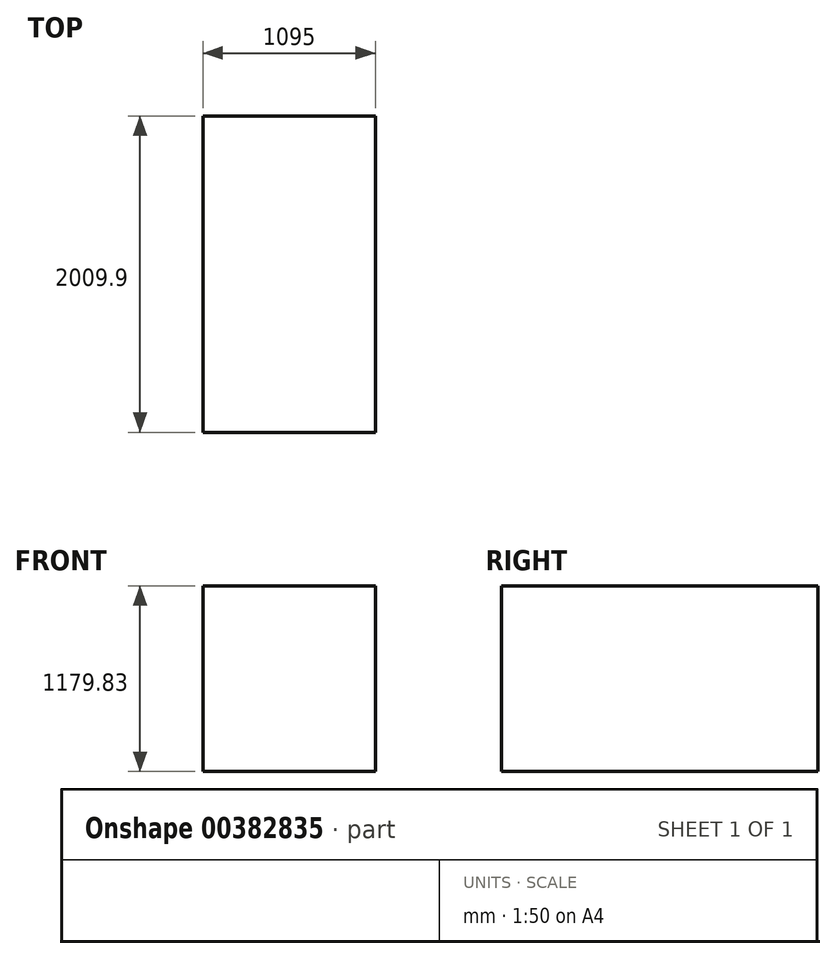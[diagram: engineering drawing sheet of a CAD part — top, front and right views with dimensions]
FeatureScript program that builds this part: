
annotation { "Feature Type Name" : "Feature", "Feature Type Description" : "" }
export const myFeature = defineFeature(function(context is Context, id is Id, definition is map)
    precondition{}
    {
        {
            var Q0;
            Q0=qCreatedBy(makeId("Front.planeOp"),FACE);
            var sketch = newSketch(context, id + "F0", { "sketchPlane" : qUnion([Q0])});
            skLineSegment(sketch, "E0.bottom", {"start": v(-547.98, 895.45) * mm, "end": v(547.02, 895.45) * mm});
            skLineSegment(sketch, "E0.top", {"start": v(-547.98, -284.38) * mm, "end": v(547.02, -284.38) * mm});
            skLineSegment(sketch, "E0.left", {"start": v(-547.98, 895.45) * mm, "end": v(-547.98, -284.38) * mm});
            skLineSegment(sketch, "E0.right", {"start": v(547.02, 895.45) * mm, "end": v(547.02, -284.38) * mm});
            skSolve(sketch);
        }
        {
            var Q0;
            Q0=makeQuery(id+"F0.imprint","IMPRINT",FACE,{"disambiguationData":[TD([[makeQuery(id+"F0.imprint","IMPRINT",EDGE,{"derivedFrom":sQuery(id+"F0.wireOp",EDGE,"E0.bottom")}),-1.0]])]});
            extrude(context, id + "F1", {"entities" : qUnion([Q0]), "endBound" : BoundingType.SYMMETRIC, "depth" : 2009.9 * mm, "offsetDistance" : 25.4 * mm});
        }
    });
